# Revit family: Cooking kettle Viking 4G 150S_4224128
name_source: partatom
category: Specialty Equipment
revit_build: Autodesk Revit 2018 (Build: 20170223_1515(x64)
units: mm (PartAtom-declared; Revit-internal decimal feet)

## family parameters
Always vertical = Yes
Cut with Voids When Loaded = No
OmniClass Number = 23.40.40.14.17.11
OmniClass Title = Cookers, Ovens, Stoves
Part Type = Normal
Room Calculation Point = No
Round Connector Dimension = Use Diameter
Shared = No
Work Plane-Based = No

## types (1)
- Cooking kettle Viking 4G 150S_4224128
    Cold Water Connection Height = 0 mm  [stored 0 ft]
    Cold Water Flow = 0.0 L/min
    Cold Water Maximum Pressure = 0.0 Pa
    Cold Water Minimum Pressure = 0.0 Pa
    Condensate Return Connection Height = 0 mm  [stored 0 ft]
    Cycle = 0 Hz
    Depth Actual = 0 mm  [stored 0 ft]
    Description = Cooking kettle Viking 4G 150S
    Description_FI = Keittopata Viking 4G 150S
    Description_NO = Kokgryte Viking 4G 150S
    Description_SE = Kokgryta Viking 4G 150S
    Direct Waste Connection Height = 0 mm  [stored 0 ft]
    Direct Waste Flow = 0.0 L/min
    Elec Conn Connection Height = 0 mm  [stored 0 ft]
    FL Amps = 0 A
    Foodservice Equipment Identifier = Yes
    Height Actual = 0 mm  [stored 0 ft]
    Hot Water Connection Height = 0 mm  [stored 0 ft]
    Hot Water Flow = 0.0 L/min
    Hot Water Maximum Pressure = 0.0 Pa
    Hot Water Minimum Pressure = 0.0 Pa
    Latent Heat Output = 0 W
    Length Actual = 0 mm  [stored 0 ft]
    Operational Current = 0 A
    Price = 0 $
    Refrigerant Mass = 0.00 kg
    Sensitive Heat Output = 0 W
    Steam Pounds per Hour = 0
    Steam Supply Connection Height = 0 mm  [stored 0 ft]
    Steam Supply Maximum Pressure = 0.0 Pa
    Steam Supply Maximum Temperature = -273 °C
    Steam Supply Minimum Pressure = 0.0 Pa
    Volts = 0 V
    Watts = 0 W
    Weight = 0

note: [stored X ft] marks values corroborated as IEEE doubles in the binary element streams (Revit-internal decimal feet)

## geometry (parser evidence)
native form markers: Sweep x2
no freeform markers — native parametric forms only
